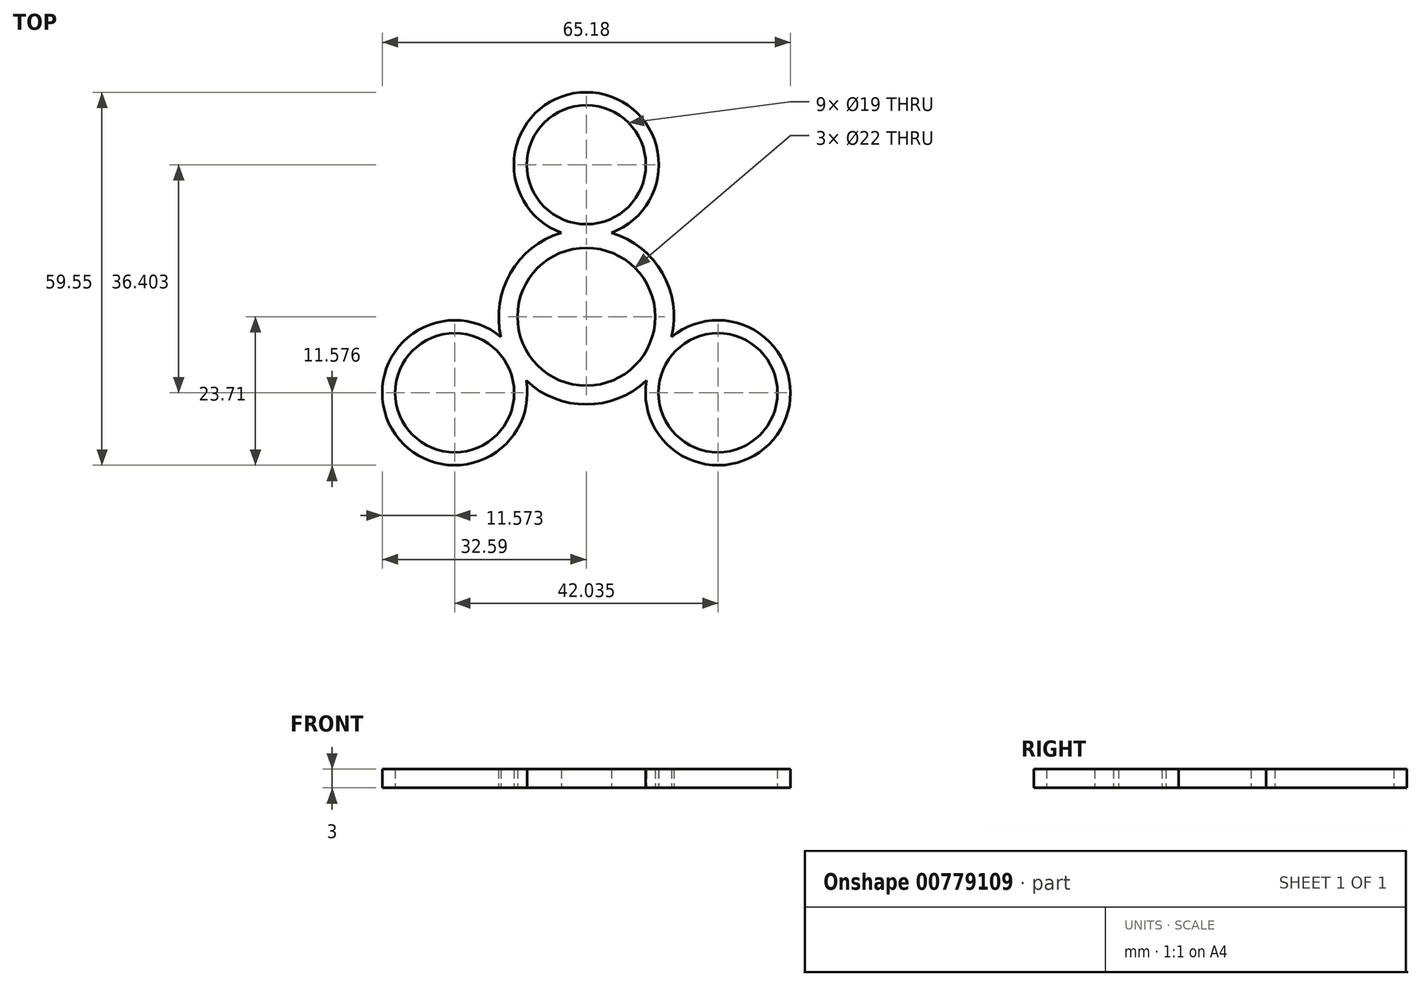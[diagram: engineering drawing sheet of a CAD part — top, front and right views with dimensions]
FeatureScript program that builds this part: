
annotation { "Feature Type Name" : "Feature", "Feature Type Description" : "" }
export const myFeature = defineFeature(function(context is Context, id is Id, definition is map)
    precondition{}
    {
        {
            var Q0;
            Q0=qCreatedBy(makeId("Top.planeOp"),FACE);
            var sketch = newSketch(context, id + "F0", { "sketchPlane" : qUnion([Q0])});
            skArc(sketch, "E0", {"start": v(9.53, 5.5) * mm, "mid": v(0, 11) * mm, "end": v(-9.53, 5.5) * mm});
            skArc(sketch, "E1", {"start": v(12.12, 7) * mm, "mid": v(8.68, 10.98) * mm, "end": v(4.01, 13.41) * mm});
            skArc(sketch, "E2", {"start": v(4.01, 13.41) * mm, "mid": v(0, 35.84) * mm, "end": v(-4.01, 13.41) * mm});
            skCircle(sketch, "E3", {"center": v(0, 24.27) * mm, "radius": 9.5 * mm});
            skArc(sketch, "E4.trimOffspring", {"start": v(-4.01, 13.41) * mm, "mid": v(-8.68, 10.98) * mm, "end": v(-12.12, 7) * mm});
            skArc(sketch, "E5.1.0", {"start": v(-13.62, -3.23) * mm, "mid": v(-31.04, -17.92) * mm, "end": v(-9.6, -10.18) * mm});
            skCircle(sketch, "E5.1.1", {"center": v(-21.02, -12.13) * mm, "radius": 9.5 * mm});
            skArc(sketch, "E5.1.2", {"start": v(-9.6, -10.18) * mm, "mid": v(-5.17, -13.01) * mm, "end": v(0, -14) * mm});
            skArc(sketch, "E5.1.3", {"start": v(-9.53, 5.5) * mm, "mid": v(-9.53, -5.5) * mm, "end": v(0, -11) * mm});
            skArc(sketch, "E5.1.4", {"start": v(-12.12, 7) * mm, "mid": v(-13.85, 2.03) * mm, "end": v(-13.62, -3.23) * mm});
            skArc(sketch, "E5.2.0", {"start": v(9.6, -10.18) * mm, "mid": v(31.04, -17.92) * mm, "end": v(13.62, -3.23) * mm});
            skCircle(sketch, "E5.2.1", {"center": v(21.02, -12.13) * mm, "radius": 9.5 * mm});
            skArc(sketch, "E5.2.2", {"start": v(13.62, -3.23) * mm, "mid": v(13.85, 2.03) * mm, "end": v(12.12, 7) * mm});
            skArc(sketch, "E5.2.3", {"start": v(0, -11) * mm, "mid": v(9.53, -5.5) * mm, "end": v(9.53, 5.5) * mm});
            skArc(sketch, "E5.2.4", {"start": v(0, -14) * mm, "mid": v(5.17, -13.01) * mm, "end": v(9.6, -10.18) * mm});
            skSolve(sketch);
        }
        {
            var Q0;
            Q0 = qSketchRegion(id + "F0", true);
            extrude(context, id + "F1", {"entities" : qUnion([Q0]), "depth" : 3 * mm, "offsetDistance" : 25 * mm});
        }
    });
